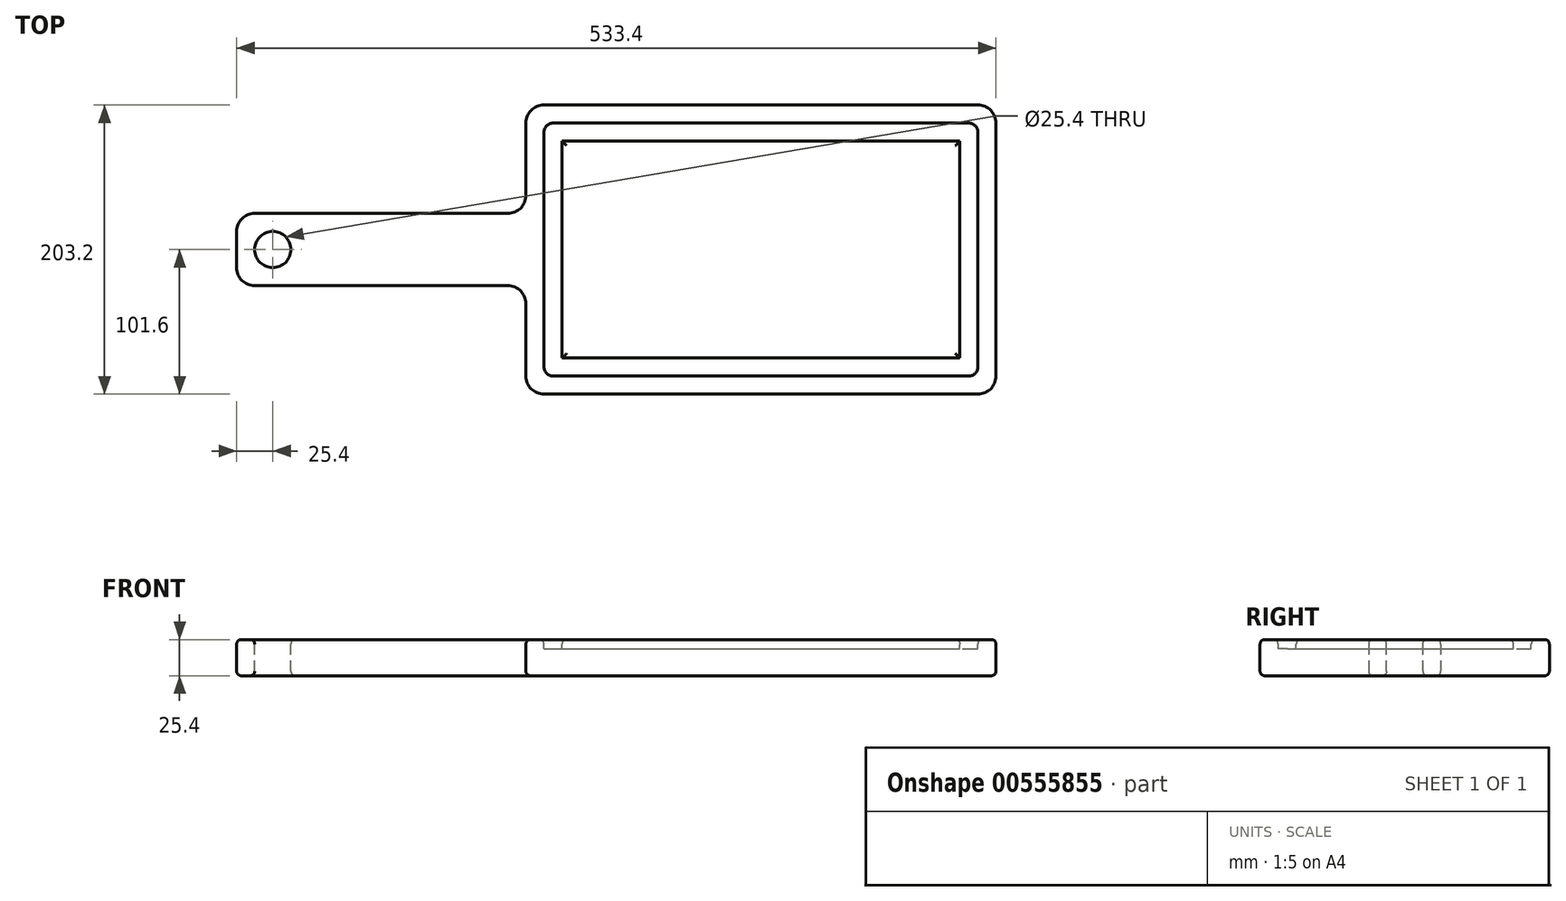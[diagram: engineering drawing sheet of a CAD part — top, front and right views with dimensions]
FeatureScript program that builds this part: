
annotation { "Feature Type Name" : "Feature", "Feature Type Description" : "" }
export const myFeature = defineFeature(function(context is Context, id is Id, definition is map)
    precondition{}
    {
        {
            var Q0;
            Q0=qCreatedBy(makeId("Top.planeOp"),FACE);
            var sketch = newSketch(context, id + "F0", { "sketchPlane" : qUnion([Q0])});
            skLineSegment(sketch, "E0.bottom", {"start": v(0, 0) * mm, "end": v(330.2, 0) * mm});
            skLineSegment(sketch, "E0.top", {"start": v(0, 203.2) * mm, "end": v(330.2, 203.2) * mm});
            skLineSegment(sketch, "E0.left", {"start": v(0, 0) * mm, "end": v(0, 203.2) * mm});
            skLineSegment(sketch, "E0.right", {"start": v(330.2, 0) * mm, "end": v(330.2, 203.2) * mm});
            skLineSegment(sketch, "E1.bottom", {"start": v(0, 127) * mm, "end": v(-203.2, 127) * mm});
            skLineSegment(sketch, "E1.top", {"start": v(0, 76.2) * mm, "end": v(-203.2, 76.2) * mm});
            skLineSegment(sketch, "E1.left", {"start": v(0, 127) * mm, "end": v(0, 76.2) * mm});
            skLineSegment(sketch, "E1.right", {"start": v(-203.2, 127) * mm, "end": v(-203.2, 76.2) * mm});
            skSolve(sketch);
        }
        {
            var Q0;
            {var subQ3=sQuery(id+"F0.wireOp",EDGE,"E0.bottom");Q0=makeQuery(id+"F0.imprint","IMPRINT",FACE,{"disambiguationData":[TD([[makeQuery(id+"F0.imprint","IMPRINT",EDGE,{"derivedFrom":subQ3}),1.0]])]});}
            var Q1;
            Q1=makeQuery(id+"F0.imprint","IMPRINT",FACE,{"disambiguationData":[TD([[makeQuery(id+"F0.imprint","IMPRINT",EDGE,{"derivedFrom":sQuery(id+"F0.wireOp",EDGE,"E1.bottom")}),1.0]])]});
            extrude(context, id + "F1", {"entities" : qUnion([Q0, Q1]), "depth" : 25.4 * mm, "offsetDistance" : 25.4 * mm});
        }
        {
            var Q0;
            Q0=makeQuery(id+"F1.opExtrude","CAP_FACE",FACE,{"disambiguationData":[OSD([sQuery(id+"F0.wireOp",EDGE,"E0.bottom"),sQuery(id+"F0.wireOp",EDGE,"E0.top"),sQuery(id+"F0.wireOp",EDGE,"E0.left"),sQuery(id+"F0.wireOp",EDGE,"E0.right"),sQuery(id+"F0.wireOp",EDGE,"E1.bottom"),sQuery(id+"F0.wireOp",EDGE,"E1.top"),sQuery(id+"F0.wireOp",EDGE,"E1.right")])],"isStart":false});
            var sketch = newSketch(context, id + "F2", { "sketchPlane" : qUnion([Q0])});
            skCircle(sketch, "E2", {"center": v(-177.8, 101.6) * mm, "radius": 12.7 * mm});
            skSolve(sketch);
        }
        {
            var Q0;
            Q0=makeQuery(id+"F2.imprint","IMPRINT",FACE,{"disambiguationData":[TD([[makeQuery(id+"F2.imprint","IMPRINT",EDGE,{"derivedFrom":sQuery(id+"F2.wireOp",EDGE,"E2")}),1.0]])]});
            extrude(context, id + "F3", {"entities" : qUnion([Q0]), "operationType" : NewBodyOperationType.REMOVE, "oppositeDirection" : true, "depth" : 25.4 * mm, "offsetDistance" : 25.4 * mm});
        }
        {
            var Q0;
            Q0=makeQuery(id+"F1.opExtrude","CAP_FACE",FACE,{"disambiguationData":[OSD([sQuery(id+"F0.wireOp",EDGE,"E0.bottom"),sQuery(id+"F0.wireOp",EDGE,"E0.top"),sQuery(id+"F0.wireOp",EDGE,"E0.left"),sQuery(id+"F0.wireOp",EDGE,"E0.right"),sQuery(id+"F0.wireOp",EDGE,"E1.bottom"),sQuery(id+"F0.wireOp",EDGE,"E1.top"),sQuery(id+"F0.wireOp",EDGE,"E1.right")])],"isStart":false});
            var sketch = newSketch(context, id + "F4", { "sketchPlane" : qUnion([Q0])});
            skLineSegment(sketch, "E3.0", {"start": v(12.7, 12.7) * mm, "end": v(12.7, 76.2) * mm});
            skLineSegment(sketch, "E3.1", {"start": v(12.7, 127) * mm, "end": v(12.7, 190.5) * mm});
            skLineSegment(sketch, "E3.2", {"start": v(12.7, 190.5) * mm, "end": v(317.5, 190.5) * mm});
            skLineSegment(sketch, "E3.3", {"start": v(317.5, 12.7) * mm, "end": v(317.5, 190.5) * mm});
            skLineSegment(sketch, "E3.4", {"start": v(12.7, 12.7) * mm, "end": v(317.5, 12.7) * mm});
            skLineSegment(sketch, "E4", {"start": v(12.7, 127) * mm, "end": v(12.7, 76.2) * mm});
            skLineSegment(sketch, "E5.0", {"start": v(25.4, 127) * mm, "end": v(25.4, 177.8) * mm});
            skLineSegment(sketch, "E5.1", {"start": v(304.8, 25.4) * mm, "end": v(304.8, 177.8) * mm});
            skLineSegment(sketch, "E5.2", {"start": v(25.4, 25.4) * mm, "end": v(304.8, 25.4) * mm});
            skLineSegment(sketch, "E5.3", {"start": v(25.4, 177.8) * mm, "end": v(304.8, 177.8) * mm});
            skLineSegment(sketch, "E5.4", {"start": v(25.4, 25.4) * mm, "end": v(25.4, 76.2) * mm});
            skLineSegment(sketch, "E5.5", {"start": v(25.4, 127) * mm, "end": v(25.4, 76.2) * mm});
            skSolve(sketch);
        }
        {
            var Q0;
            Q0=makeQuery(id+"F4.imprint","IMPRINT",FACE,{"disambiguationData":[TD([[makeQuery(id+"F4.imprint","IMPRINT",EDGE,{"derivedFrom":sQuery(id+"F4.wireOp",EDGE,"E3.0")}),-1.0]])]});
            extrude(context, id + "F5", {"entities" : qUnion([Q0]), "operationType" : NewBodyOperationType.REMOVE, "oppositeDirection" : true, "depth" : 6.35 * mm, "offsetDistance" : 25.4 * mm});
        }
        {
            var Q0;
            Q0=makeQuery(id+"F5.boolean.opBoolean","COPY",EDGE,{"derivedFrom":makeQuery(id+"F5.opExtrude","SWEPT_EDGE",EDGE,{"disambiguationData":[OSD([sQuery(id+"F4.wireOp",EDGE,"E3.1"),sQuery(id+"F4.wireOp",EDGE,"E3.2")])]})});
            var Q1;
            Q1=makeQuery(id+"F5.boolean.opBoolean","COPY",EDGE,{"derivedFrom":makeQuery(id+"F5.opExtrude","SWEPT_EDGE",EDGE,{"disambiguationData":[OSD([sQuery(id+"F4.wireOp",EDGE,"E3.2"),sQuery(id+"F4.wireOp",EDGE,"E3.3")])]})});
            var Q2;
            Q2=makeQuery(id+"F5.boolean.opBoolean","COPY",EDGE,{"derivedFrom":makeQuery(id+"F5.opExtrude","SWEPT_EDGE",EDGE,{"disambiguationData":[OSD([sQuery(id+"F4.wireOp",EDGE,"E3.3"),sQuery(id+"F4.wireOp",EDGE,"E3.4")])]})});
            var Q3;
            Q3=makeQuery(id+"F5.boolean.opBoolean","COPY",EDGE,{"derivedFrom":makeQuery(id+"F5.opExtrude","SWEPT_EDGE",EDGE,{"disambiguationData":[OSD([sQuery(id+"F4.wireOp",EDGE,"E3.0"),sQuery(id+"F4.wireOp",EDGE,"E3.4")])]})});
            fillet(context, id + "F6", {"entities" : qUnion([Q0, Q1, Q2, Q3]), "radius" : 6.35 * mm, "tangentPropagation" : true, "allowEdgeOverflow" : false});
        }
        {
            var Q0;
            Q0=makeQuery(id+"F1.opExtrude","SWEPT_EDGE",EDGE,{"disambiguationData":[OSD([sQuery(id+"F0.wireOp",EDGE,"E0.top"),sQuery(id+"F0.wireOp",EDGE,"E0.left")])]});
            var Q1;
            Q1=makeQuery(id+"F1.opExtrude","SWEPT_EDGE",EDGE,{"disambiguationData":[OSD([sQuery(id+"F0.wireOp",EDGE,"E0.left"),sQuery(id+"F0.wireOp",EDGE,"E1.bottom"),sQuery(id+"F0.wireOp",EDGE,"E1.left")])]});
            var Q2;
            Q2=makeQuery(id+"F1.opExtrude","SWEPT_EDGE",EDGE,{"disambiguationData":[OSD([sQuery(id+"F0.wireOp",EDGE,"E1.bottom"),sQuery(id+"F0.wireOp",EDGE,"E1.right")])]});
            var Q3;
            Q3=makeQuery(id+"F1.opExtrude","SWEPT_EDGE",EDGE,{"disambiguationData":[OSD([sQuery(id+"F0.wireOp",EDGE,"E1.top"),sQuery(id+"F0.wireOp",EDGE,"E1.right")])]});
            var Q4;
            Q4=makeQuery(id+"F1.opExtrude","SWEPT_EDGE",EDGE,{"disambiguationData":[OSD([sQuery(id+"F0.wireOp",EDGE,"E0.left"),sQuery(id+"F0.wireOp",EDGE,"E1.top"),sQuery(id+"F0.wireOp",EDGE,"E1.left")])]});
            var Q5;
            Q5=makeQuery(id+"F1.opExtrude","SWEPT_EDGE",EDGE,{"disambiguationData":[OSD([sQuery(id+"F0.wireOp",EDGE,"E0.bottom"),sQuery(id+"F0.wireOp",EDGE,"E0.left")])]});
            var Q6;
            Q6=makeQuery(id+"F1.opExtrude","SWEPT_EDGE",EDGE,{"disambiguationData":[OSD([sQuery(id+"F0.wireOp",EDGE,"E0.top"),sQuery(id+"F0.wireOp",EDGE,"E0.right")])]});
            var Q7;
            Q7=makeQuery(id+"F1.opExtrude","SWEPT_EDGE",EDGE,{"disambiguationData":[OSD([sQuery(id+"F0.wireOp",EDGE,"E0.bottom"),sQuery(id+"F0.wireOp",EDGE,"E0.right")])]});
            fillet(context, id + "F7", {"entities" : qUnion([Q0, Q1, Q2, Q3, Q4, Q5, Q6, Q7]), "radius" : 12.7 * mm, "tangentPropagation" : true, "allowEdgeOverflow" : false});
        }
        {
            var Q0;
            Q0=makeQuery(id+"F5.boolean.opBoolean","SPLIT",FACE,{"disambiguationData":[TD([makeQuery(id+"F5.opExtrude","SWEPT_FACE",FACE,{"disambiguationData":[OSD([sQuery(id+"F4.wireOp",EDGE,"E5.1")])]})])],"derivedFrom":makeQuery(id+"F1.opExtrude","CAP_FACE",FACE,{"disambiguationData":[OSD([sQuery(id+"F0.wireOp",EDGE,"E0.bottom"),sQuery(id+"F0.wireOp",EDGE,"E0.top"),sQuery(id+"F0.wireOp",EDGE,"E0.left"),sQuery(id+"F0.wireOp",EDGE,"E0.right"),sQuery(id+"F0.wireOp",EDGE,"E1.bottom"),sQuery(id+"F0.wireOp",EDGE,"E1.top"),sQuery(id+"F0.wireOp",EDGE,"E1.right")])],"isStart":false})});
            var Q1;
            {var subQ0=sQuery(id+"F0.wireOp",EDGE,"E0.left");var subQ1=sQuery(id+"F0.wireOp",EDGE,"E0.top");var subQ3=sQuery(id+"F0.wireOp",EDGE,"E1.bottom");var subQ4=sQuery(id+"F0.wireOp",EDGE,"E1.right");var subQ5=sQuery(id+"F0.wireOp",EDGE,"E1.top");var subQ6=sQuery(id+"F0.wireOp",EDGE,"E0.right");var subQ7=sQuery(id+"F0.wireOp",EDGE,"E0.bottom");Q1=makeQuery(id+"F5.boolean.opBoolean","SPLIT",FACE,{"disambiguationData":[TD([makeQuery(id+"F1.opExtrude","SWEPT_FACE",FACE,{"disambiguationData":[OSD([subQ7])]})])],"derivedFrom":makeQuery(id+"F1.opExtrude","CAP_FACE",FACE,{"disambiguationData":[OSD([subQ7,subQ1,subQ0,subQ6,subQ3,subQ5,subQ4])],"isStart":false})});}
            var Q2;
            Q2=makeQuery(id+"F1.opExtrude","CAP_FACE",FACE,{"disambiguationData":[OSD([sQuery(id+"F0.wireOp",EDGE,"E0.bottom"),sQuery(id+"F0.wireOp",EDGE,"E0.top"),sQuery(id+"F0.wireOp",EDGE,"E0.left"),sQuery(id+"F0.wireOp",EDGE,"E0.right"),sQuery(id+"F0.wireOp",EDGE,"E1.bottom"),sQuery(id+"F0.wireOp",EDGE,"E1.top"),sQuery(id+"F0.wireOp",EDGE,"E1.right")])],"isStart":true});
            fillet(context, id + "F8", {"entities" : qUnion([Q0, Q1, Q2]), "radius" : 3.17 * mm, "tangentPropagation" : true, "allowEdgeOverflow" : false});
        }
    });
